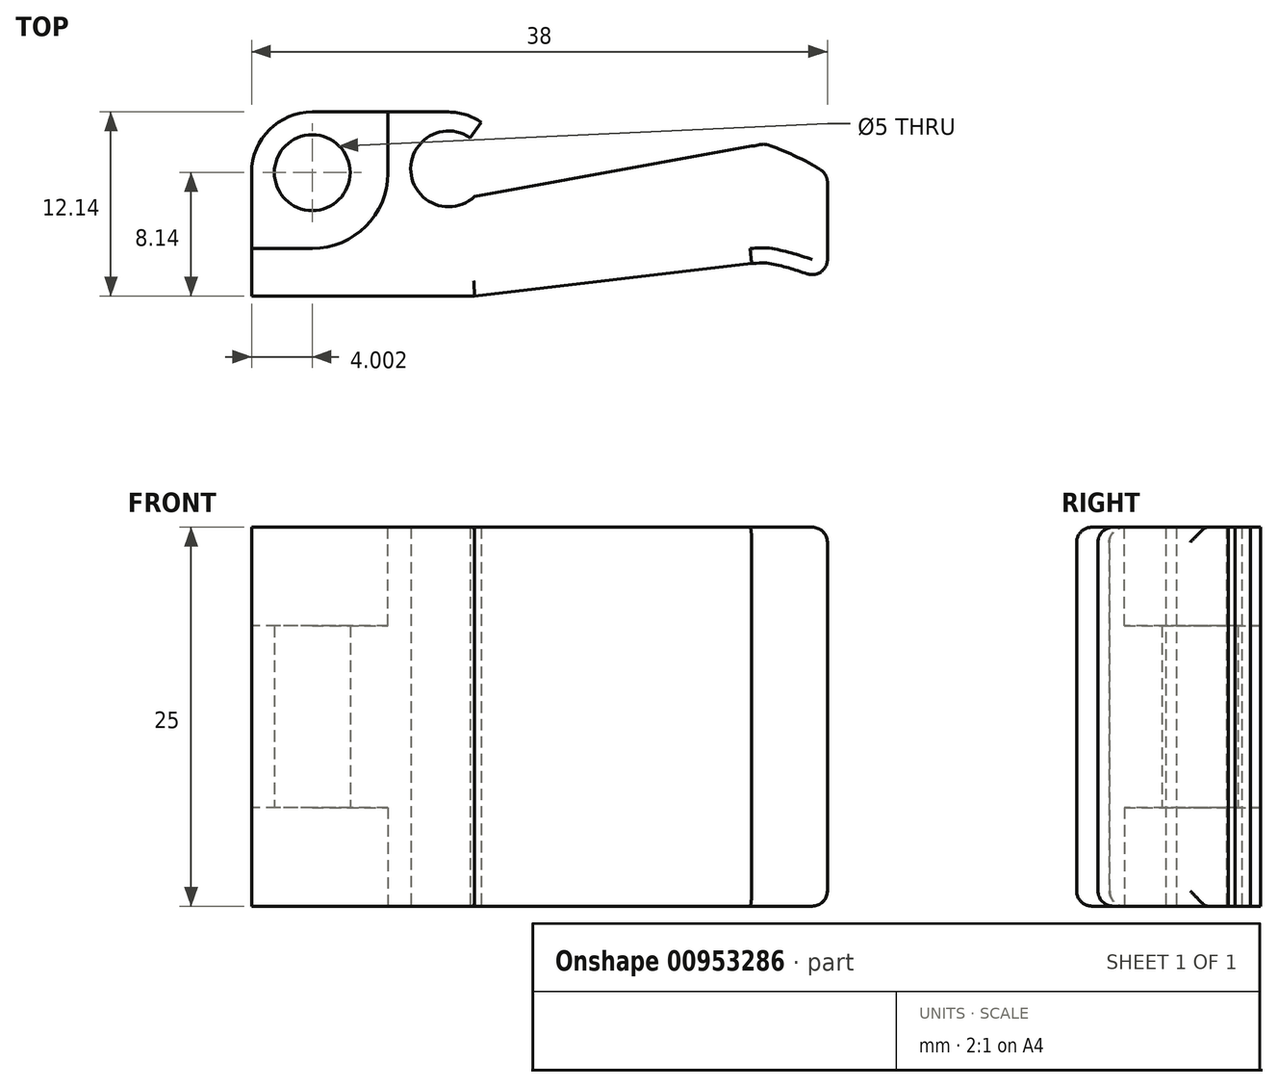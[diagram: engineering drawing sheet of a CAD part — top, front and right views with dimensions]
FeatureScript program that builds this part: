
annotation { "Feature Type Name" : "Feature", "Feature Type Description" : "" }
export const myFeature = defineFeature(function(context is Context, id is Id, definition is map)
    precondition{}
    {
        {
            var Q0;
            Q0=qCreatedBy(makeId("Top.planeOp"),FACE);
            var sketch = newSketch(context, id + "F0", { "sketchPlane" : qUnion([Q0])});
            skLineSegment(sketch, "E0", {"start": v(1.67, 10) * mm, "end": v(-11.33, 10) * mm});
            skLineSegment(sketch, "E1", {"start": v(-11.33, 10) * mm, "end": v(-11.33, 0) * mm});
            skCircle(sketch, "E2", {"center": v(-7.33, 6) * mm, "radius": 2.5 * mm});
            skArc(sketch, "E3", {"start": v(-7.33, 10) * mm, "mid": v(-10.16, 8.83) * mm, "end": v(-11.33, 6) * mm});
            skCircle(sketch, "E4", {"center": v(1.67, 6.25) * mm, "radius": 2.5 * mm, "construction": true});
            skArc(sketch, "E5", {"start": v(1.67, 10) * mm, "mid": v(2.8, 9.83) * mm, "end": v(3.83, 9.32) * mm});
            skArc(sketch, "E6", {"start": v(1.67, 3.75) * mm, "mid": v(2.6, 3.93) * mm, "end": v(3.4, 4.43) * mm});
            skArc(sketch, "E7", {"start": v(1.67, 3.75) * mm, "mid": v(-0.72, 7) * mm, "end": v(3.09, 8.31) * mm});
            skLineSegment(sketch, "E8", {"start": v(3.09, 8.31) * mm, "end": v(3.83, 9.32) * mm});
            skLineSegment(sketch, "E9", {"start": v(21.67, 0) * mm, "end": v(3.4, -2.14) * mm});
            skLineSegment(sketch, "E10", {"start": v(3.4, -2.14) * mm, "end": v(-11.33, -2.14) * mm});
            skLineSegment(sketch, "E11", {"start": v(-11.33, -2.14) * mm, "end": v(-11.33, 0) * mm});
            skLineSegment(sketch, "E12", {"start": v(3.4, 4.43) * mm, "end": v(21.67, 7.75) * mm});
            skFitSpline(sketch, "E13", {"points": [v(21.67, 7.75) * mm, v(22.72, 7.83) * mm, v(26.67, 5.83) * mm], "startDerivative": vector(5.47, 0.72) * mm, "endDerivative": vector(2.52, -2.71) * mm});
            skFitSpline(sketch, "E14", {"points": [v(21.67, 0) * mm, v(22.9, 0) * mm, v(26.67, -1.17) * mm], "startDerivative": vector(2.53, 0.22) * mm, "endDerivative": vector(2.48, -1.14) * mm});
            skLineSegment(sketch, "E15", {"start": v(26.67, -1.17) * mm, "end": v(26.67, 5.83) * mm});
            skSolve(sketch);
        }
        {
            var Q0;
            Q0=makeQuery(id+"F0.imprint","IMPRINT",FACE,{"disambiguationData":[TD([[makeQuery(id+"F0.imprint","IMPRINT",EDGE,{"derivedFrom":sQuery(id+"F0.wireOp",EDGE,"E2")}),-1.0]])]});
            extrude(context, id + "F1", {"entities" : qUnion([Q0]), "depth" : 25 * mm, "offsetDistance" : 25 * mm});
        }
        {
            var Q0;
            Q0=makeQuery(id+"F1.opExtrude","CAP_FACE",FACE,{"disambiguationData":[OSD([sQuery(id+"F0.wireOp",EDGE,"E0"),sQuery(id+"F0.wireOp",EDGE,"E1"),sQuery(id+"F0.wireOp",EDGE,"E2"),sQuery(id+"F0.wireOp",EDGE,"E3"),sQuery(id+"F0.wireOp",EDGE,"E5"),sQuery(id+"F0.wireOp",EDGE,"E6"),sQuery(id+"F0.wireOp",EDGE,"E7"),sQuery(id+"F0.wireOp",EDGE,"E8"),sQuery(id+"F0.wireOp",EDGE,"E9"),sQuery(id+"F0.wireOp",EDGE,"E10"),sQuery(id+"F0.wireOp",EDGE,"E11"),sQuery(id+"F0.wireOp",EDGE,"E12"),sQuery(id+"F0.wireOp",EDGE,"E13"),sQuery(id+"F0.wireOp",EDGE,"E14"),sQuery(id+"F0.wireOp",EDGE,"E15")])],"isStart":false});
            var sketch = newSketch(context, id + "F2", { "sketchPlane" : qUnion([Q0])});
            skLineSegment(sketch, "E16", {"start": v(-2.33, 5.96) * mm, "end": v(-2.33, 10) * mm});
            skArc(sketch, "E17", {"start": v(-2.33, 5.96) * mm, "mid": v(-3.8, 2.45) * mm, "end": v(-7.33, 1) * mm});
            skLineSegment(sketch, "E18", {"start": v(-7.33, 1) * mm, "end": v(-11.33, 1) * mm});
            skSolve(sketch);
        }
        {
            var Q0;
            {var subQ2=sQuery(id+"F2.wireOp",EDGE,"E16");Q0=makeQuery(id+"F2.imprint","IMPRINT",FACE,{"disambiguationData":[TD([[makeQuery(id+"F2.imprint","IMPRINT",EDGE,{"derivedFrom":subQ2}),1.0]])]});}
            extrude(context, id + "F3", {"entities" : qUnion([Q0]), "operationType" : NewBodyOperationType.ADD, "oppositeDirection" : true, "depth" : 30 * mm, "offsetDistance" : 25 * mm});
        }
        {
            var Q0;
            {var subQ1=sQuery(id+"F2.wireOp",EDGE,"E16");Q0=makeQuery(id+"F2.imprint","IMPRINT",FACE,{"disambiguationData":[TD([[makeQuery(id+"F2.imprint","IMPRINT",EDGE,{"derivedFrom":subQ1}),1.0]])]});}
            extrude(context, id + "F4", {"entities" : qUnion([Q0]), "operationType" : NewBodyOperationType.REMOVE, "oppositeDirection" : true, "depth" : 6.5 * mm, "offsetDistance" : 25 * mm});
        }
        {
            var Q0;
            Q0=makeQuery(id+"F3.opExtrude","CAP_FACE",FACE,{"disambiguationData":[OSD([sQuery(id+"F0.wireOp",EDGE,"E0"),sQuery(id+"F0.wireOp",EDGE,"E1"),sQuery(id+"F0.wireOp",EDGE,"E2"),sQuery(id+"F0.wireOp",EDGE,"E3"),sQuery(id+"F0.wireOp",EDGE,"E11"),sQuery(id+"F2.wireOp",EDGE,"E16"),sQuery(id+"F2.wireOp",EDGE,"E17"),sQuery(id+"F2.wireOp",EDGE,"E18")])],"isStart":false});
            extrude(context, id + "F5", {"entities" : qUnion([Q0]), "operationType" : NewBodyOperationType.REMOVE, "oppositeDirection" : true, "depth" : 11.5 * mm, "offsetDistance" : 25 * mm});
        }
        {
            var Q0;
            Q0=makeQuery(id+"F1.opExtrude","SWEPT_EDGE",EDGE,{"disambiguationData":[OSD([sQuery(id+"F0.wireOp",EDGE,"E13"),sQuery(id+"F0.wireOp",EDGE,"E15")])]});
            var Q1;
            Q1=makeQuery(id+"F1.opExtrude","SWEPT_EDGE",EDGE,{"disambiguationData":[OSD([sQuery(id+"F0.wireOp",EDGE,"E14"),sQuery(id+"F0.wireOp",EDGE,"E15")])]});
            var Q2;
            Q2=makeQuery(id+"F1.opExtrude","CAP_EDGE",EDGE,{"disambiguationData":[OSD([sQuery(id+"F0.wireOp",EDGE,"E9")])],"isStart":false});
            var Q3;
            Q3=makeQuery(id+"F1.opExtrude","CAP_EDGE",EDGE,{"disambiguationData":[OSD([sQuery(id+"F0.wireOp",EDGE,"E9")])],"isStart":true});
            var Q4;
            Q4=makeQuery(id+"F1.opExtrude","CAP_EDGE",EDGE,{"disambiguationData":[OSD([sQuery(id+"F0.wireOp",EDGE,"E15")])],"isStart":false});
            var Q5;
            Q5=makeQuery(id+"F1.opExtrude","CAP_EDGE",EDGE,{"disambiguationData":[OSD([sQuery(id+"F0.wireOp",EDGE,"E15")])],"isStart":true});
            var Q6;
            Q6=makeQuery(id+"F1.opExtrude","CAP_EDGE",EDGE,{"disambiguationData":[OSD([sQuery(id+"F0.wireOp",EDGE,"E10")])],"isStart":true});
            var Q7;
            Q7=makeQuery(id+"F1.opExtrude","CAP_EDGE",EDGE,{"disambiguationData":[OSD([sQuery(id+"F0.wireOp",EDGE,"E10")])],"isStart":false});
            fillet(context, id + "F6", {"entities" : qUnion([Q0, Q1, Q2, Q3, Q4, Q5, Q6, Q7]), "radius" : 1 * mm, "tangentPropagation" : true, "allowEdgeOverflow" : false});
        }
    });
